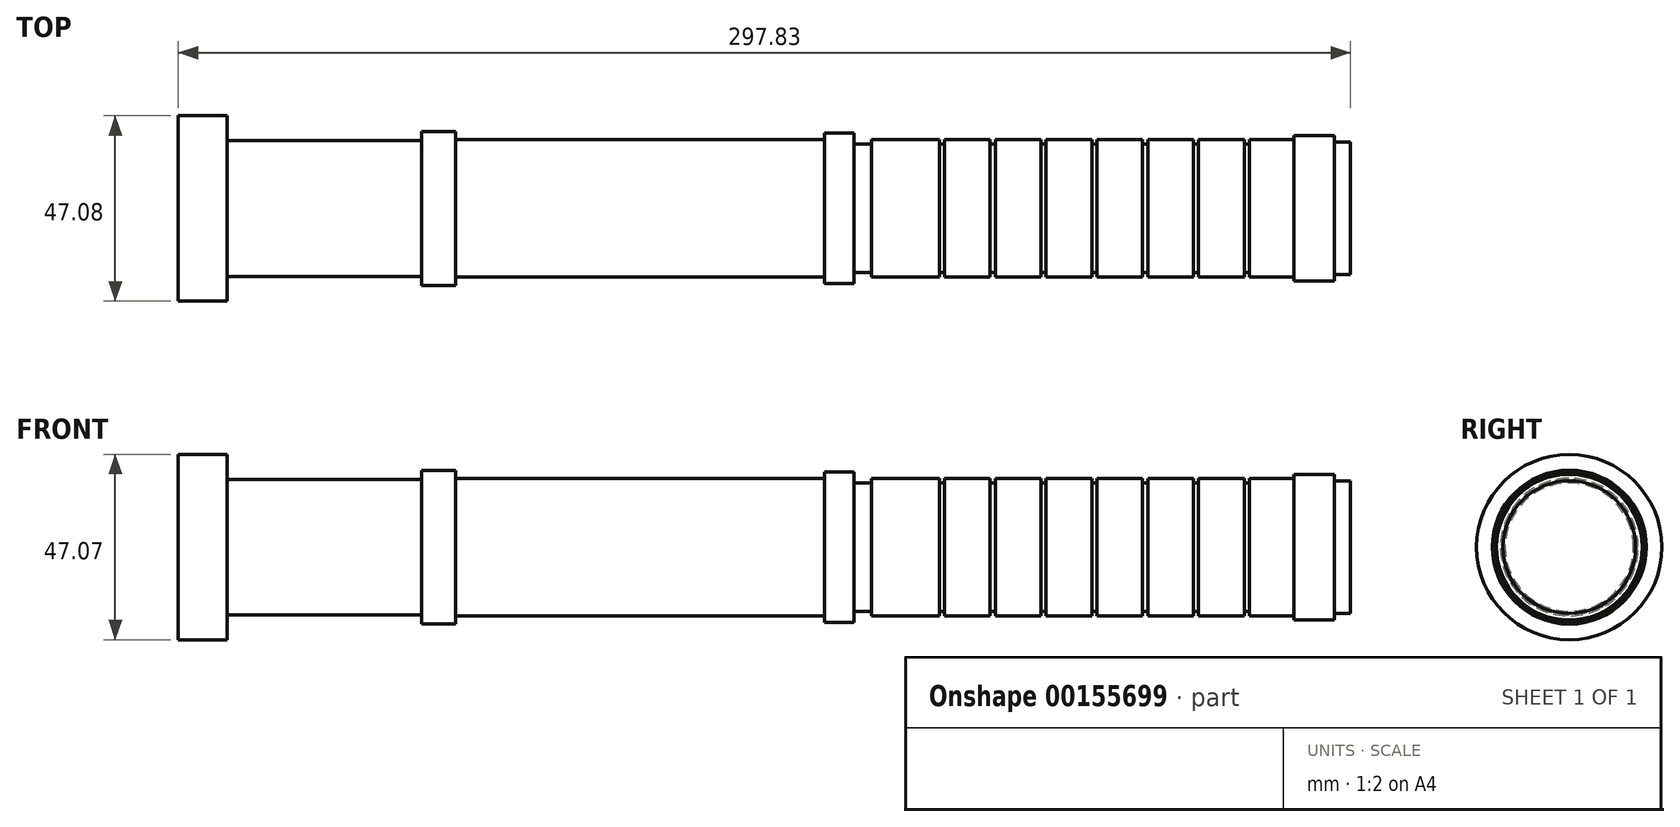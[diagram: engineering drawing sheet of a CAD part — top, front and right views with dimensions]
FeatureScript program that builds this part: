
annotation { "Feature Type Name" : "Feature", "Feature Type Description" : "" }
export const myFeature = defineFeature(function(context is Context, id is Id, definition is map)
    precondition{}
    {
        {
            var Q0;
            Q0=qCreatedBy(makeId("Front.planeOp"),FACE);
            var sketch = newSketch(context, id + "F0", { "sketchPlane" : qUnion([Q0])});
            skLineSegment(sketch, "E0", {"start": v(13.13, -55) * mm, "end": v(313.04, -55) * mm});
            skLineSegment(sketch, "E1", {"start": v(313.04, -55) * mm, "end": v(313.04, -38.15) * mm});
            skLineSegment(sketch, "E2", {"start": v(313.04, -38.15) * mm, "end": v(308.98, -38.15) * mm});
            skLineSegment(sketch, "E3", {"start": v(308.98, -38.15) * mm, "end": v(308.98, -36.49) * mm});
            skLineSegment(sketch, "E4", {"start": v(308.98, -36.49) * mm, "end": v(298.64, -36.49) * mm});
            skLineSegment(sketch, "E5", {"start": v(298.64, -36.49) * mm, "end": v(298.64, -37.53) * mm});
            skLineSegment(sketch, "E6", {"start": v(298.64, -37.53) * mm, "end": v(287.33, -37.53) * mm});
            skLineSegment(sketch, "E7", {"start": v(287.33, -37.53) * mm, "end": v(287.33, -38.67) * mm});
            skLineSegment(sketch, "E8", {"start": v(287.33, -38.67) * mm, "end": v(286, -38.67) * mm});
            skLineSegment(sketch, "E9", {"start": v(286, -38.67) * mm, "end": v(286, -37.53) * mm});
            skLineSegment(sketch, "E10", {"start": v(286, -37.53) * mm, "end": v(274.42, -37.53) * mm});
            skLineSegment(sketch, "E11", {"start": v(274.42, -37.53) * mm, "end": v(274.42, -38.67) * mm});
            skLineSegment(sketch, "E12", {"start": v(274.42, -38.67) * mm, "end": v(273.1, -38.67) * mm});
            skLineSegment(sketch, "E13", {"start": v(273.1, -38.67) * mm, "end": v(273.1, -37.53) * mm});
            skLineSegment(sketch, "E14", {"start": v(273.1, -37.53) * mm, "end": v(261.51, -37.53) * mm});
            skLineSegment(sketch, "E15", {"start": v(261.51, -37.53) * mm, "end": v(261.51, -38.67) * mm});
            skLineSegment(sketch, "E16", {"start": v(261.51, -38.67) * mm, "end": v(260.18, -38.67) * mm});
            skLineSegment(sketch, "E17", {"start": v(260.18, -38.67) * mm, "end": v(260.18, -37.53) * mm});
            skLineSegment(sketch, "E18", {"start": v(260.18, -37.53) * mm, "end": v(248.6, -37.53) * mm});
            skLineSegment(sketch, "E19", {"start": v(248.6, -37.53) * mm, "end": v(248.6, -38.67) * mm});
            skLineSegment(sketch, "E20", {"start": v(248.6, -38.67) * mm, "end": v(247.28, -38.67) * mm});
            skLineSegment(sketch, "E21", {"start": v(247.28, -38.67) * mm, "end": v(247.28, -37.53) * mm});
            skLineSegment(sketch, "E22", {"start": v(247.28, -37.53) * mm, "end": v(235.7, -37.53) * mm});
            skLineSegment(sketch, "E23", {"start": v(235.7, -37.53) * mm, "end": v(235.7, -38.67) * mm});
            skLineSegment(sketch, "E24", {"start": v(235.7, -38.67) * mm, "end": v(234.37, -38.67) * mm});
            skLineSegment(sketch, "E25", {"start": v(234.37, -38.67) * mm, "end": v(234.37, -37.53) * mm});
            skLineSegment(sketch, "E26", {"start": v(234.37, -37.53) * mm, "end": v(222.8, -37.53) * mm});
            skLineSegment(sketch, "E27", {"start": v(222.8, -37.53) * mm, "end": v(222.8, -38.67) * mm});
            skLineSegment(sketch, "E28", {"start": v(222.8, -38.67) * mm, "end": v(221.46, -38.67) * mm});
            skLineSegment(sketch, "E29", {"start": v(221.46, -38.67) * mm, "end": v(221.46, -37.53) * mm});
            skLineSegment(sketch, "E30", {"start": v(221.46, -37.53) * mm, "end": v(209.89, -37.53) * mm});
            skLineSegment(sketch, "E31", {"start": v(209.89, -37.53) * mm, "end": v(209.89, -38.67) * mm});
            skLineSegment(sketch, "E32", {"start": v(209.89, -38.67) * mm, "end": v(208.56, -38.67) * mm});
            skLineSegment(sketch, "E33", {"start": v(208.56, -38.67) * mm, "end": v(208.56, -37.53) * mm});
            skLineSegment(sketch, "E34", {"start": v(208.56, -37.53) * mm, "end": v(191.34, -37.53) * mm});
            skLineSegment(sketch, "E35", {"start": v(191.34, -37.53) * mm, "end": v(191.34, -38.67) * mm});
            skLineSegment(sketch, "E36", {"start": v(191.34, -38.67) * mm, "end": v(186.91, -38.67) * mm});
            skLineSegment(sketch, "E37", {"start": v(186.91, -38.67) * mm, "end": v(186.91, -35.9) * mm});
            skLineSegment(sketch, "E38", {"start": v(186.91, -35.9) * mm, "end": v(179.32, -35.9) * mm});
            skLineSegment(sketch, "E39", {"start": v(179.32, -35.9) * mm, "end": v(179.32, -37.52) * mm});
            skLineSegment(sketch, "E40", {"start": v(179.32, -37.52) * mm, "end": v(85.65, -37.52) * mm});
            skLineSegment(sketch, "E41", {"start": v(85.65, -37.52) * mm, "end": v(85.65, -35.45) * mm});
            skLineSegment(sketch, "E42", {"start": v(85.65, -35.45) * mm, "end": v(77.02, -35.45) * mm});
            skLineSegment(sketch, "E43", {"start": v(77.02, -35.45) * mm, "end": v(77.02, -37.75) * mm});
            skLineSegment(sketch, "E44", {"start": v(77.02, -37.75) * mm, "end": v(27.58, -37.75) * mm});
            skLineSegment(sketch, "E45", {"start": v(27.58, -37.75) * mm, "end": v(27.58, -31.46) * mm});
            skLineSegment(sketch, "E46", {"start": v(27.58, -31.46) * mm, "end": v(15.21, -31.46) * mm});
            skLineSegment(sketch, "E47", {"start": v(15.21, -31.46) * mm, "end": v(15.21, -55) * mm});
            skSolve(sketch);
        }
        {
            var Q0;
            Q0 = qSketchRegion(id + "F0", true);
            var Q1;
            Q1=sQuery(id+"F0.wireOp",EDGE,"E0");
            revolve(context, id + "F1", {"entities" : qUnion([Q0]), "axis" : qUnion([Q1]), "revolveType" : RevolveType.FULL});
        }
    });
